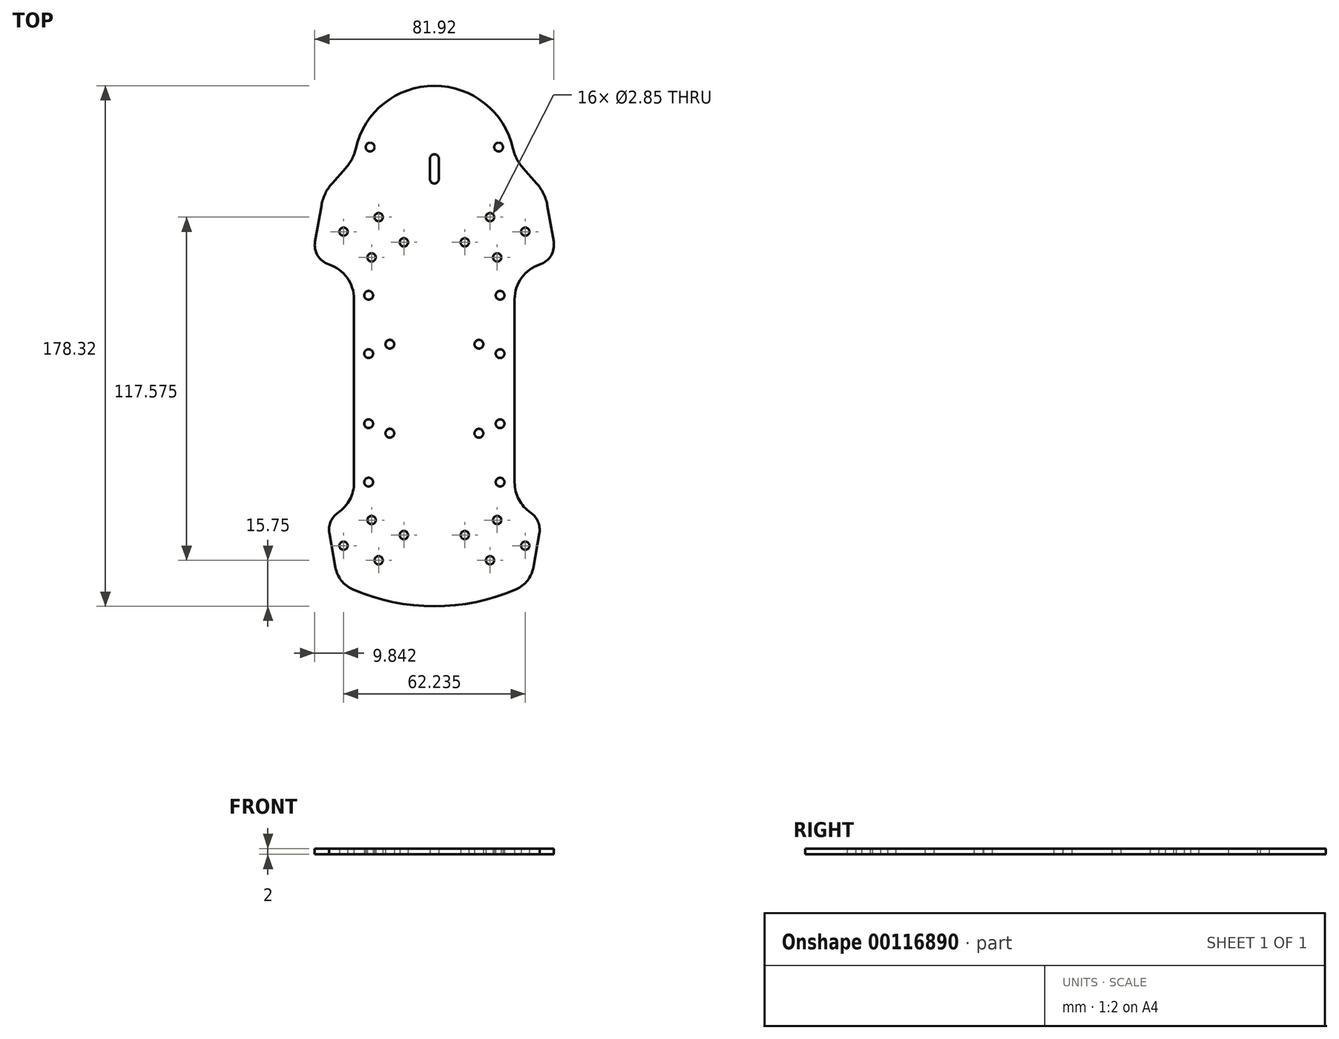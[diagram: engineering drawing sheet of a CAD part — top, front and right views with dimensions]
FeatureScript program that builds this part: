
annotation { "Feature Type Name" : "Feature", "Feature Type Description" : "" }
export const myFeature = defineFeature(function(context is Context, id is Id, definition is map)
    precondition{}
    {
        {
            var Q0;
            Q0=qCreatedBy(makeId("Top.planeOp"),FACE);
            var sketch = newSketch(context, id + "F0", { "sketchPlane" : qUnion([Q0])});
            skLineSegment(sketch, "E0", {"start": v(-27.15, 153.46) * mm, "end": v(-17.3, 155.2) * mm});
            skLineSegment(sketch, "E1", {"start": v(-17.3, 155.2) * mm, "end": v(-14.87, 141.4) * mm});
            skLineSegment(sketch, "E2", {"start": v(-14.87, 141.4) * mm, "end": v(-24.72, 139.67) * mm});
            skLineSegment(sketch, "E3", {"start": v(-24.72, 139.67) * mm, "end": v(-27.15, 153.46) * mm});
            skLineSegment(sketch, "E4", {"start": v(-8.87, 175.2) * mm, "end": v(-8.87, 29.62) * mm});
            skLineSegment(sketch, "E5", {"start": v(-63.87, 175.2) * mm, "end": v(-63.87, 29.62) * mm});
            skCircle(sketch, "E6", {"center": v(-51.62, 111.66) * mm, "radius": 1.5 * mm});
            skCircle(sketch, "E7", {"center": v(-21.12, 111.66) * mm, "radius": 1.5 * mm});
            skCircle(sketch, "E8", {"center": v(-51.62, 81.16) * mm, "radius": 1.5 * mm});
            skCircle(sketch, "E9", {"center": v(-21.12, 81.16) * mm, "radius": 1.5 * mm});
            skCircle(sketch, "E10", {"center": v(-17.3, 155.2) * mm, "radius": 1.43 * mm});
            skCircle(sketch, "E11", {"center": v(-27.15, 153.46) * mm, "radius": 1.43 * mm});
            skCircle(sketch, "E12", {"center": v(-24.72, 139.67) * mm, "radius": 1.43 * mm});
            skCircle(sketch, "E13", {"center": v(-14.87, 141.4) * mm, "radius": 1.43 * mm});
            skLineSegment(sketch, "E14", {"start": v(-63.87, 175.2) * mm, "end": v(-8.87, 175.2) * mm});
            skLineSegment(sketch, "E15", {"start": v(-45.6, 153.46) * mm, "end": v(-55.44, 155.2) * mm});
            skLineSegment(sketch, "E16", {"start": v(-55.44, 155.2) * mm, "end": v(-57.87, 141.4) * mm});
            skLineSegment(sketch, "E17", {"start": v(-57.87, 141.4) * mm, "end": v(-48.02, 139.67) * mm});
            skLineSegment(sketch, "E18", {"start": v(-48.02, 139.67) * mm, "end": v(-45.6, 153.46) * mm});
            skCircle(sketch, "E19", {"center": v(-55.44, 155.2) * mm, "radius": 1.43 * mm});
            skCircle(sketch, "E20", {"center": v(-45.6, 153.46) * mm, "radius": 1.43 * mm});
            skCircle(sketch, "E21", {"center": v(-48.02, 139.67) * mm, "radius": 1.43 * mm});
            skCircle(sketch, "E22", {"center": v(-57.87, 141.4) * mm, "radius": 1.43 * mm});
            skLineSegment(sketch, "E23", {"start": v(-63.87, 29.62) * mm, "end": v(-8.87, 29.62) * mm});
            skLineSegment(sketch, "E24.bottom", {"start": v(-54.37, 114.4) * mm, "end": v(-18.37, 114.4) * mm});
            skLineSegment(sketch, "E24.top", {"start": v(-54.37, 78.4) * mm, "end": v(-18.37, 78.4) * mm});
            skLineSegment(sketch, "E24.left", {"start": v(-54.37, 114.4) * mm, "end": v(-54.37, 78.4) * mm});
            skLineSegment(sketch, "E24.right", {"start": v(-18.37, 114.4) * mm, "end": v(-18.37, 78.4) * mm});
            skLineSegment(sketch, "E25", {"start": v(-57.87, 51.4) * mm, "end": v(-48.02, 53.14) * mm});
            skLineSegment(sketch, "E26", {"start": v(-48.02, 53.14) * mm, "end": v(-45.6, 39.36) * mm});
            skLineSegment(sketch, "E27", {"start": v(-45.6, 39.36) * mm, "end": v(-55.44, 37.62) * mm});
            skLineSegment(sketch, "E28", {"start": v(-55.44, 37.62) * mm, "end": v(-57.87, 51.4) * mm});
            skLineSegment(sketch, "E29", {"start": v(-24.72, 53.14) * mm, "end": v(-14.87, 51.4) * mm});
            skLineSegment(sketch, "E30", {"start": v(-14.87, 51.4) * mm, "end": v(-17.3, 37.62) * mm});
            skLineSegment(sketch, "E31", {"start": v(-17.3, 37.62) * mm, "end": v(-27.15, 39.36) * mm});
            skLineSegment(sketch, "E32", {"start": v(-27.15, 39.36) * mm, "end": v(-24.72, 53.14) * mm});
            skCircle(sketch, "E33", {"center": v(-57.87, 51.4) * mm, "radius": 1.43 * mm});
            skCircle(sketch, "E34", {"center": v(-48.02, 53.14) * mm, "radius": 1.43 * mm});
            skCircle(sketch, "E35", {"center": v(-45.6, 39.36) * mm, "radius": 1.43 * mm});
            skCircle(sketch, "E36", {"center": v(-55.44, 37.62) * mm, "radius": 1.43 * mm});
            skCircle(sketch, "E37", {"center": v(-27.15, 39.36) * mm, "radius": 1.43 * mm});
            skCircle(sketch, "E38", {"center": v(-24.72, 53.14) * mm, "radius": 1.43 * mm});
            skCircle(sketch, "E39", {"center": v(-14.87, 51.4) * mm, "radius": 1.43 * mm});
            skCircle(sketch, "E40", {"center": v(-17.3, 37.62) * mm, "radius": 1.43 * mm});
            skLineSegment(sketch, "E41", {"start": v(-74.29, 163.48) * mm, "end": v(-39.3, 157.93) * mm});
            skLineSegment(sketch, "E42", {"start": v(-39.3, 157.93) * mm, "end": v(-43.63, 133.31) * mm});
            skLineSegment(sketch, "E43", {"start": v(-43.63, 133.31) * mm, "end": v(-71.66, 138.76) * mm});
            skLineSegment(sketch, "E44", {"start": v(-77.22, 146.85) * mm, "end": v(-75.03, 159.3) * mm});
            skLineSegment(sketch, "E45", {"start": v(-36.37, 175.2) * mm, "end": v(-36.37, 125.27) * mm});
            skLineSegment(sketch, "E46.MirrorCS", {"start": v(1.55, 163.48) * mm, "end": v(-33.45, 157.93) * mm});
            skLineSegment(sketch, "E47.MirrorCS", {"start": v(-33.45, 157.93) * mm, "end": v(-29.1, 133.31) * mm});
            skLineSegment(sketch, "E48.MirrorCS", {"start": v(-29.1, 133.31) * mm, "end": v(-1.08, 138.76) * mm});
            skLineSegment(sketch, "E49.MirrorCS", {"start": v(4.48, 146.85) * mm, "end": v(2.28, 159.3) * mm});
            skPoint(sketch, "E50", {"position": v(-36.37, 200.2) * mm});
            skArc(sketch, "E51", {"start": v(-9.42, 178.63) * mm, "mid": v(-36.37, 200.2) * mm, "end": v(-63.32, 178.63) * mm});
            skLineSegment(sketch, "E52", {"start": v(-71.46, 166.65) * mm, "end": v(-66.74, 171.96) * mm});
            skLineSegment(sketch, "E53", {"start": v(-6, 171.96) * mm, "end": v(-1.28, 166.65) * mm});
            skCircle(sketch, "E54", {"center": v(-36.37, 175.2) * mm, "radius": 1.5 * mm});
            skPoint(sketch, "E55.visualSharp", {"position": v(-78.41, 140.07) * mm});
            skArc(sketch, "E55.filletArc", {"start": v(-77.22, 146.85) * mm, "mid": v(-76.1, 141.67) * mm, "end": v(-71.66, 138.76) * mm});
            skPoint(sketch, "E56.visualSharp", {"position": v(5.67, 140.07) * mm});
            skArc(sketch, "E56.filletArc", {"start": v(-1.08, 138.76) * mm, "mid": v(3.35, 141.67) * mm, "end": v(4.48, 146.85) * mm});
            skPoint(sketch, "E57.visualSharp", {"position": v(-74.29, 163.48) * mm});
            skArc(sketch, "E57.filletArc", {"start": v(-71.46, 166.65) * mm, "mid": v(-73.76, 163.22) * mm, "end": v(-75.03, 159.3) * mm});
            skPoint(sketch, "E58.visualSharp", {"position": v(-63.87, 175.2) * mm});
            skArc(sketch, "E58.filletArc", {"start": v(-66.74, 171.96) * mm, "mid": v(-64.6, 175.08) * mm, "end": v(-63.32, 178.63) * mm});
            skPoint(sketch, "E59.visualSharp", {"position": v(-8.87, 175.2) * mm});
            skArc(sketch, "E59.filletArc", {"start": v(-9.42, 178.63) * mm, "mid": v(-8.13, 175.08) * mm, "end": v(-6, 171.96) * mm});
            skPoint(sketch, "E60.visualSharp", {"position": v(1.55, 163.48) * mm});
            skArc(sketch, "E60.filletArc", {"start": v(2.28, 159.3) * mm, "mid": v(1.02, 163.22) * mm, "end": v(-1.28, 166.65) * mm});
            skCircle(sketch, "E61", {"center": v(-76.37, 127.1) * mm, "radius": 12.5 * mm});
            skCircle(sketch, "E62", {"center": v(3.63, 127.1) * mm, "radius": 12.5 * mm});
            skLineSegment(sketch, "E63", {"start": v(-54.37, 96.4) * mm, "end": v(-95.75, 96.4) * mm});
            skPoint(sketch, "E63.endSnap0", {"position": v(-54.37, 96.4) * mm});
            skLineSegment(sketch, "E64.MirrorCS", {"start": v(-33.45, 34.88) * mm, "end": v(-29.1, 59.5) * mm});
            skLineSegment(sketch, "E65", {"start": v(-29.1, 59.5) * mm, "end": v(-5.99, 55) * mm});
            skLineSegment(sketch, "E66", {"start": v(-0.43, 46.92) * mm, "end": v(-2.5, 35.15) * mm});
            skLineSegment(sketch, "E67", {"start": v(-3.4, 30.12) * mm, "end": v(-33.45, 34.88) * mm});
            skLineSegment(sketch, "E68.MirrorCS", {"start": v(-39.3, 34.88) * mm, "end": v(-43.63, 59.5) * mm});
            skLineSegment(sketch, "E69.MirrorCS", {"start": v(-43.63, 59.5) * mm, "end": v(-66.75, 55) * mm});
            skLineSegment(sketch, "E70.MirrorCS", {"start": v(-69.35, 30.12) * mm, "end": v(-39.3, 34.88) * mm});
            skLineSegment(sketch, "E71.MirrorCS", {"start": v(-72.31, 46.92) * mm, "end": v(-70.23, 35.15) * mm});
            skArc(sketch, "E72", {"start": v(-64.39, 27.72) * mm, "mid": v(-36.37, 21.87) * mm, "end": v(-8.35, 27.72) * mm});
            skCircle(sketch, "E73", {"center": v(-76.37, 64.27) * mm, "radius": 12.5 * mm});
            skCircle(sketch, "E74", {"center": v(3.63, 64.27) * mm, "radius": 12.5 * mm});
            skPoint(sketch, "E75.visualSharp", {"position": v(-73.5, 53.7) * mm});
            skArc(sketch, "E75.filletArc", {"start": v(-66.75, 55) * mm, "mid": v(-71.19, 52.1) * mm, "end": v(-72.31, 46.92) * mm});
            skPoint(sketch, "E76.visualSharp", {"position": v(0.76, 53.7) * mm});
            skArc(sketch, "E76.filletArc", {"start": v(-0.43, 46.92) * mm, "mid": v(-1.55, 52.1) * mm, "end": v(-5.99, 55) * mm});
            skPoint(sketch, "E77.visualSharp", {"position": v(-69.35, 30.12) * mm});
            skArc(sketch, "E77.filletArc", {"start": v(-70.23, 35.15) * mm, "mid": v(-68.24, 30.7) * mm, "end": v(-64.39, 27.72) * mm});
            skPoint(sketch, "E78.visualSharp", {"position": v(-3.4, 30.12) * mm});
            skArc(sketch, "E78.filletArc", {"start": v(-8.35, 27.72) * mm, "mid": v(-4.5, 30.7) * mm, "end": v(-2.5, 35.15) * mm});
            skCircle(sketch, "E79", {"center": v(-58.87, 128.4) * mm, "radius": 1.5 * mm});
            skCircle(sketch, "E80", {"center": v(-58.87, 108.4) * mm, "radius": 1.5 * mm});
            skCircle(sketch, "E81", {"center": v(-58.87, 84.4) * mm, "radius": 1.5 * mm});
            skCircle(sketch, "E82", {"center": v(-58.87, 64.4) * mm, "radius": 1.5 * mm});
            skCircle(sketch, "E83.MirrorC", {"center": v(-13.87, 128.4) * mm, "radius": 1.5 * mm});
            skCircle(sketch, "E84.MirrorC", {"center": v(-13.87, 108.4) * mm, "radius": 1.5 * mm});
            skCircle(sketch, "E85.MirrorC", {"center": v(-13.87, 84.4) * mm, "radius": 1.5 * mm});
            skCircle(sketch, "E86.MirrorC", {"center": v(-13.87, 64.4) * mm, "radius": 1.5 * mm});
            skCircle(sketch, "E87", {"center": v(-58.37, 179.2) * mm, "radius": 1.5 * mm});
            skCircle(sketch, "E88", {"center": v(-14.37, 179.2) * mm, "radius": 1.5 * mm});
            skLineSegment(sketch, "E89", {"start": v(-56.65, 148.3) * mm, "end": v(-67.49, 150.21) * mm});
            skCircle(sketch, "E90", {"center": v(-67.49, 150.21) * mm, "radius": 1.43 * mm});
            skCircle(sketch, "E91.MirrorC", {"center": v(-5.25, 150.21) * mm, "radius": 1.43 * mm});
            skCircle(sketch, "E92.MirrorC", {"center": v(-67.49, 42.6) * mm, "radius": 1.43 * mm});
            skCircle(sketch, "E93.MirrorC", {"center": v(-5.25, 42.6) * mm, "radius": 1.43 * mm});
            skCircle(sketch, "E94", {"center": v(-46.8, 146.56) * mm, "radius": 1.43 * mm});
            skCircle(sketch, "E95.MirrorC", {"center": v(-25.93, 146.56) * mm, "radius": 1.43 * mm});
            skCircle(sketch, "E96.MirrorC", {"center": v(-46.8, 46.25) * mm, "radius": 1.43 * mm});
            skCircle(sketch, "E97.MirrorC", {"center": v(-25.93, 46.25) * mm, "radius": 1.43 * mm});
            skCircle(sketch, "E98", {"center": v(-36.37, 168.2) * mm, "radius": 1.5 * mm});
            skLineSegment(sketch, "E99", {"start": v(-37.87, 178.57) * mm, "end": v(-37.87, 162.7) * mm});
            skLineSegment(sketch, "E100", {"start": v(-34.87, 178.97) * mm, "end": v(-34.87, 161.55) * mm});
            skSolve(sketch);
        }
        {
            var Q0;
            Q0=makeQuery(id+"F0.imprint","IMPRINT",FACE,{"disambiguationData":[TD([[makeQuery(id+"F0.imprint","IMPRINT",EDGE,{"derivedFrom":sQuery(id+"F0.wireOp",EDGE,"E23")}),-1.0]])]});
            var Q1;
            {var subQ0=sQuery(id+"F0.wireOp",EDGE,"E62");var subQ1=sQuery(id+"F0.wireOp",EDGE,"E56.filletArc");var subQ3=makeQuery(id+"F0.imprint","INTERSECT",VERTEX,{"derivedFrom":[subQ1,subQ0]});Q1=makeQuery(id+"F0.imprint","IMPRINT",FACE,{"disambiguationData":[TD([[makeQuery(id+"F0.imprint","IMPRINT",EDGE,{"disambiguationData":[TD([[subQ3,1.0]])],"derivedFrom":subQ1}),1.0]])]});}
            var Q2;
            {var subQ0=sQuery(id+"F0.wireOp",EDGE,"E62");var subQ1=sQuery(id+"F0.wireOp",EDGE,"E4");var subQ2=makeQuery(id+"F0.imprint","INTERSECT",VERTEX,{"derivedFrom":[subQ1,subQ0]});Q2=makeQuery(id+"F0.imprint","IMPRINT",FACE,{"disambiguationData":[TD([[makeQuery(id+"F0.imprint","IMPRINT",EDGE,{"disambiguationData":[TD([[subQ2,1.0]])],"derivedFrom":subQ1}),1.0]])]});}
            var Q3;
            {var subQ0=sQuery(id+"F0.wireOp",EDGE,"E61");var subQ1=sQuery(id+"F0.wireOp",EDGE,"E5");var subQ2=makeQuery(id+"F0.imprint","INTERSECT",VERTEX,{"derivedFrom":[subQ1,subQ0]});Q3=makeQuery(id+"F0.imprint","IMPRINT",FACE,{"disambiguationData":[TD([[makeQuery(id+"F0.imprint","IMPRINT",EDGE,{"disambiguationData":[TD([[subQ2,1.0]])],"derivedFrom":subQ1}),-1.0]])]});}
            var Q4;
            Q4=makeQuery(id+"F0.imprint","IMPRINT",FACE,{"disambiguationData":[TD([[makeQuery(id+"F0.imprint","IMPRINT",EDGE,{"derivedFrom":sQuery(id+"F0.wireOp",EDGE,"E51")}),1.0]])]});
            var Q5;
            {var subQ0=sQuery(id+"F0.wireOp",EDGE,"E49.MirrorCS");Q5=makeQuery(id+"F0.imprint","IMPRINT",FACE,{"disambiguationData":[TD([[makeQuery(id+"F0.imprint","IMPRINT",EDGE,{"derivedFrom":subQ0}),1.0]])]});}
            var Q6;
            {var subQ0=sQuery(id+"F0.wireOp",EDGE,"E44");Q6=makeQuery(id+"F0.imprint","IMPRINT",FACE,{"disambiguationData":[TD([[makeQuery(id+"F0.imprint","IMPRINT",EDGE,{"derivedFrom":subQ0}),-1.0]])]});}
            var Q7;
            {var subQ29=sQuery(id+"F0.wireOp",EDGE,"E23");Q7=makeQuery(id+"F0.imprint","IMPRINT",FACE,{"disambiguationData":[TD([[makeQuery(id+"F0.imprint","IMPRINT",EDGE,{"derivedFrom":subQ29}),1.0]])]});}
            var Q8;
            {var subQ3=sQuery(id+"F0.wireOp",EDGE,"E20");var subQ13=sQuery(id+"F0.wireOp",EDGE,"E15");var subQ14=makeQuery(id+"F0.imprint","INTERSECT",VERTEX,{"derivedFrom":[subQ13,subQ3]});Q8=makeQuery(id+"F0.imprint","IMPRINT",FACE,{"disambiguationData":[TD([[makeQuery(id+"F0.imprint","IMPRINT",EDGE,{"disambiguationData":[TD([[subQ14,-1.0]])],"derivedFrom":subQ13}),1.0]])]});}
            var Q9;
            {var subQ3=sQuery(id+"F0.wireOp",EDGE,"E11");var subQ13=sQuery(id+"F0.wireOp",EDGE,"E0");var subQ14=makeQuery(id+"F0.imprint","INTERSECT",VERTEX,{"derivedFrom":[subQ13,subQ3]});Q9=makeQuery(id+"F0.imprint","IMPRINT",FACE,{"disambiguationData":[TD([[makeQuery(id+"F0.imprint","IMPRINT",EDGE,{"disambiguationData":[TD([[subQ14,-1.0]])],"derivedFrom":subQ13}),-1.0]])]});}
            var Q10;
            Q10=makeQuery(id+"F0.imprint","IMPRINT",FACE,{"disambiguationData":[TD([[makeQuery(id+"F0.imprint","IMPRINT",EDGE,{"derivedFrom":sQuery(id+"F0.wireOp",EDGE,"E6")}),-1.0]])]});
            var Q11;
            {var subQ3=sQuery(id+"F0.wireOp",EDGE,"E33");var subQ13=sQuery(id+"F0.wireOp",EDGE,"E25");var subQ14=makeQuery(id+"F0.imprint","INTERSECT",VERTEX,{"derivedFrom":[subQ13,subQ3]});Q11=makeQuery(id+"F0.imprint","IMPRINT",FACE,{"disambiguationData":[TD([[makeQuery(id+"F0.imprint","IMPRINT",EDGE,{"disambiguationData":[TD([[subQ14,-1.0]])],"derivedFrom":subQ13}),-1.0]])]});}
            var Q12;
            {var subQ3=sQuery(id+"F0.wireOp",EDGE,"E38");var subQ13=sQuery(id+"F0.wireOp",EDGE,"E29");var subQ14=makeQuery(id+"F0.imprint","INTERSECT",VERTEX,{"derivedFrom":[subQ13,subQ3]});Q12=makeQuery(id+"F0.imprint","IMPRINT",FACE,{"disambiguationData":[TD([[makeQuery(id+"F0.imprint","IMPRINT",EDGE,{"disambiguationData":[TD([[subQ14,-1.0]])],"derivedFrom":subQ13}),-1.0]])]});}
            var Q13;
            {var subQ0=sQuery(id+"F0.wireOp",EDGE,"E42");Q13=makeQuery(id+"F0.imprint","IMPRINT",FACE,{"disambiguationData":[TD([[makeQuery(id+"F0.imprint","IMPRINT",EDGE,{"derivedFrom":subQ0}),-1.0]])]});}
            var Q14;
            {var subQ0=sQuery(id+"F0.wireOp",EDGE,"E47.MirrorCS");Q14=makeQuery(id+"F0.imprint","IMPRINT",FACE,{"disambiguationData":[TD([[makeQuery(id+"F0.imprint","IMPRINT",EDGE,{"derivedFrom":subQ0}),1.0]])]});}
            var Q15;
            {var subQ0=sQuery(id+"F0.wireOp",EDGE,"E61");var subQ1=sQuery(id+"F0.wireOp",EDGE,"E55.filletArc");var subQ3=makeQuery(id+"F0.imprint","INTERSECT",VERTEX,{"derivedFrom":[subQ1,subQ0]});Q15=makeQuery(id+"F0.imprint","IMPRINT",FACE,{"disambiguationData":[TD([[makeQuery(id+"F0.imprint","IMPRINT",EDGE,{"disambiguationData":[TD([[subQ3,-1.0]])],"derivedFrom":subQ1}),1.0]])]});}
            var Q16;
            {var subQ0=sQuery(id+"F0.wireOp",EDGE,"E74");var subQ1=sQuery(id+"F0.wireOp",EDGE,"E4");var subQ2=makeQuery(id+"F0.imprint","INTERSECT",VERTEX,{"derivedFrom":[subQ1,subQ0]});Q16=makeQuery(id+"F0.imprint","IMPRINT",FACE,{"disambiguationData":[TD([[makeQuery(id+"F0.imprint","IMPRINT",EDGE,{"disambiguationData":[TD([[subQ2,-1.0]])],"derivedFrom":subQ1}),1.0]])]});}
            var Q17;
            {var subQ10=sQuery(id+"F0.wireOp",EDGE,"E66");Q17=makeQuery(id+"F0.imprint","IMPRINT",FACE,{"disambiguationData":[TD([[makeQuery(id+"F0.imprint","IMPRINT",EDGE,{"derivedFrom":subQ10}),-1.0]])]});}
            var Q18;
            {var subQ0=sQuery(id+"F0.wireOp",EDGE,"E64.MirrorCS");Q18=makeQuery(id+"F0.imprint","IMPRINT",FACE,{"disambiguationData":[TD([[makeQuery(id+"F0.imprint","IMPRINT",EDGE,{"derivedFrom":subQ0}),-1.0]])]});}
            var Q19;
            {var subQ0=sQuery(id+"F0.wireOp",EDGE,"E68.MirrorCS");Q19=makeQuery(id+"F0.imprint","IMPRINT",FACE,{"disambiguationData":[TD([[makeQuery(id+"F0.imprint","IMPRINT",EDGE,{"derivedFrom":subQ0}),1.0]])]});}
            var Q20;
            {var subQ0=sQuery(id+"F0.wireOp",EDGE,"E71.MirrorCS");Q20=makeQuery(id+"F0.imprint","IMPRINT",FACE,{"disambiguationData":[TD([[makeQuery(id+"F0.imprint","IMPRINT",EDGE,{"derivedFrom":subQ0}),1.0]])]});}
            var Q21;
            {var subQ0=sQuery(id+"F0.wireOp",EDGE,"E73");var subQ1=sQuery(id+"F0.wireOp",EDGE,"E5");var subQ2=makeQuery(id+"F0.imprint","INTERSECT",VERTEX,{"derivedFrom":[subQ1,subQ0]});Q21=makeQuery(id+"F0.imprint","IMPRINT",FACE,{"disambiguationData":[TD([[makeQuery(id+"F0.imprint","IMPRINT",EDGE,{"disambiguationData":[TD([[subQ2,-1.0]])],"derivedFrom":subQ1}),-1.0]])]});}
            var Q22;
            {var subQ0=sQuery(id+"F0.wireOp",EDGE,"E18");var subQ1=sQuery(id+"F0.wireOp",EDGE,"E15");var subQ2=makeQuery(id+"F0.imprint","INTERSECT",VERTEX,{"derivedFrom":[subQ1,subQ0]});Q22=makeQuery(id+"F0.imprint","IMPRINT",FACE,{"disambiguationData":[TD([[makeQuery(id+"F0.imprint","IMPRINT",EDGE,{"disambiguationData":[TD([[subQ2,-1.0]])],"derivedFrom":subQ1}),1.0]])]});}
            var Q23;
            {var subQ0=sQuery(id+"F0.wireOp",EDGE,"E18");var subQ1=sQuery(id+"F0.wireOp",EDGE,"E15");var subQ2=makeQuery(id+"F0.imprint","INTERSECT",VERTEX,{"derivedFrom":[subQ1,subQ0]});Q23=makeQuery(id+"F0.imprint","IMPRINT",FACE,{"disambiguationData":[TD([[makeQuery(id+"F0.imprint","IMPRINT",EDGE,{"disambiguationData":[TD([[subQ2,-1.0]])],"derivedFrom":subQ1}),-1.0]])]});}
            var Q24;
            {var subQ0=sQuery(id+"F0.wireOp",EDGE,"E18");var subQ1=sQuery(id+"F0.wireOp",EDGE,"E17");var subQ2=makeQuery(id+"F0.imprint","INTERSECT",VERTEX,{"derivedFrom":[subQ1,subQ0]});Q24=makeQuery(id+"F0.imprint","IMPRINT",FACE,{"disambiguationData":[TD([[makeQuery(id+"F0.imprint","IMPRINT",EDGE,{"disambiguationData":[TD([[subQ2,1.0]])],"derivedFrom":subQ1}),1.0]])]});}
            var Q25;
            {var subQ0=sQuery(id+"F0.wireOp",EDGE,"E18");var subQ1=sQuery(id+"F0.wireOp",EDGE,"E17");var subQ2=makeQuery(id+"F0.imprint","INTERSECT",VERTEX,{"derivedFrom":[subQ1,subQ0]});Q25=makeQuery(id+"F0.imprint","IMPRINT",FACE,{"disambiguationData":[TD([[makeQuery(id+"F0.imprint","IMPRINT",EDGE,{"disambiguationData":[TD([[subQ2,1.0]])],"derivedFrom":subQ1}),-1.0]])]});}
            var Q26;
            {var subQ0=sQuery(id+"F0.wireOp",EDGE,"E3");var subQ1=sQuery(id+"F0.wireOp",EDGE,"E0");var subQ2=makeQuery(id+"F0.imprint","INTERSECT",VERTEX,{"derivedFrom":[subQ1,subQ0]});Q26=makeQuery(id+"F0.imprint","IMPRINT",FACE,{"disambiguationData":[TD([[makeQuery(id+"F0.imprint","IMPRINT",EDGE,{"disambiguationData":[TD([[subQ2,-1.0]])],"derivedFrom":subQ1}),-1.0]])]});}
            var Q27;
            {var subQ0=sQuery(id+"F0.wireOp",EDGE,"E3");var subQ1=sQuery(id+"F0.wireOp",EDGE,"E0");var subQ2=makeQuery(id+"F0.imprint","INTERSECT",VERTEX,{"derivedFrom":[subQ1,subQ0]});Q27=makeQuery(id+"F0.imprint","IMPRINT",FACE,{"disambiguationData":[TD([[makeQuery(id+"F0.imprint","IMPRINT",EDGE,{"disambiguationData":[TD([[subQ2,-1.0]])],"derivedFrom":subQ1}),1.0]])]});}
            var Q28;
            {var subQ0=sQuery(id+"F0.wireOp",EDGE,"E3");var subQ1=sQuery(id+"F0.wireOp",EDGE,"E2");var subQ2=makeQuery(id+"F0.imprint","INTERSECT",VERTEX,{"derivedFrom":[subQ1,subQ0]});Q28=makeQuery(id+"F0.imprint","IMPRINT",FACE,{"disambiguationData":[TD([[makeQuery(id+"F0.imprint","IMPRINT",EDGE,{"disambiguationData":[TD([[subQ2,1.0]])],"derivedFrom":subQ1}),1.0]])]});}
            var Q29;
            {var subQ0=sQuery(id+"F0.wireOp",EDGE,"E3");var subQ1=sQuery(id+"F0.wireOp",EDGE,"E2");var subQ2=makeQuery(id+"F0.imprint","INTERSECT",VERTEX,{"derivedFrom":[subQ1,subQ0]});Q29=makeQuery(id+"F0.imprint","IMPRINT",FACE,{"disambiguationData":[TD([[makeQuery(id+"F0.imprint","IMPRINT",EDGE,{"disambiguationData":[TD([[subQ2,1.0]])],"derivedFrom":subQ1}),-1.0]])]});}
            var Q30;
            {var subQ0=sQuery(id+"F0.wireOp",EDGE,"E26");var subQ1=sQuery(id+"F0.wireOp",EDGE,"E25");var subQ2=makeQuery(id+"F0.imprint","INTERSECT",VERTEX,{"derivedFrom":[subQ1,subQ0]});Q30=makeQuery(id+"F0.imprint","IMPRINT",FACE,{"disambiguationData":[TD([[makeQuery(id+"F0.imprint","IMPRINT",EDGE,{"disambiguationData":[TD([[subQ2,1.0]])],"derivedFrom":subQ1}),1.0]])]});}
            var Q31;
            {var subQ0=sQuery(id+"F0.wireOp",EDGE,"E26");var subQ1=sQuery(id+"F0.wireOp",EDGE,"E25");var subQ2=makeQuery(id+"F0.imprint","INTERSECT",VERTEX,{"derivedFrom":[subQ1,subQ0]});Q31=makeQuery(id+"F0.imprint","IMPRINT",FACE,{"disambiguationData":[TD([[makeQuery(id+"F0.imprint","IMPRINT",EDGE,{"disambiguationData":[TD([[subQ2,1.0]])],"derivedFrom":subQ1}),-1.0]])]});}
            var Q32;
            {var subQ0=sQuery(id+"F0.wireOp",EDGE,"E27");var subQ1=sQuery(id+"F0.wireOp",EDGE,"E26");var subQ2=makeQuery(id+"F0.imprint","INTERSECT",VERTEX,{"derivedFrom":[subQ1,subQ0]});Q32=makeQuery(id+"F0.imprint","IMPRINT",FACE,{"disambiguationData":[TD([[makeQuery(id+"F0.imprint","IMPRINT",EDGE,{"disambiguationData":[TD([[subQ2,1.0]])],"derivedFrom":subQ1}),-1.0]])]});}
            var Q33;
            {var subQ0=sQuery(id+"F0.wireOp",EDGE,"E27");var subQ1=sQuery(id+"F0.wireOp",EDGE,"E26");var subQ2=makeQuery(id+"F0.imprint","INTERSECT",VERTEX,{"derivedFrom":[subQ1,subQ0]});Q33=makeQuery(id+"F0.imprint","IMPRINT",FACE,{"disambiguationData":[TD([[makeQuery(id+"F0.imprint","IMPRINT",EDGE,{"disambiguationData":[TD([[subQ2,1.0]])],"derivedFrom":subQ1}),1.0]])]});}
            var Q34;
            {var subQ0=sQuery(id+"F0.wireOp",EDGE,"E32");var subQ1=sQuery(id+"F0.wireOp",EDGE,"E29");var subQ2=makeQuery(id+"F0.imprint","INTERSECT",VERTEX,{"derivedFrom":[subQ1,subQ0]});Q34=makeQuery(id+"F0.imprint","IMPRINT",FACE,{"disambiguationData":[TD([[makeQuery(id+"F0.imprint","IMPRINT",EDGE,{"disambiguationData":[TD([[subQ2,-1.0]])],"derivedFrom":subQ1}),1.0]])]});}
            var Q35;
            {var subQ0=sQuery(id+"F0.wireOp",EDGE,"E32");var subQ1=sQuery(id+"F0.wireOp",EDGE,"E29");var subQ2=makeQuery(id+"F0.imprint","INTERSECT",VERTEX,{"derivedFrom":[subQ1,subQ0]});Q35=makeQuery(id+"F0.imprint","IMPRINT",FACE,{"disambiguationData":[TD([[makeQuery(id+"F0.imprint","IMPRINT",EDGE,{"disambiguationData":[TD([[subQ2,-1.0]])],"derivedFrom":subQ1}),-1.0]])]});}
            var Q36;
            {var subQ0=sQuery(id+"F0.wireOp",EDGE,"E32");var subQ1=sQuery(id+"F0.wireOp",EDGE,"E31");var subQ2=makeQuery(id+"F0.imprint","INTERSECT",VERTEX,{"derivedFrom":[subQ1,subQ0]});Q36=makeQuery(id+"F0.imprint","IMPRINT",FACE,{"disambiguationData":[TD([[makeQuery(id+"F0.imprint","IMPRINT",EDGE,{"disambiguationData":[TD([[subQ2,1.0]])],"derivedFrom":subQ1}),-1.0]])]});}
            var Q37;
            {var subQ0=sQuery(id+"F0.wireOp",EDGE,"E32");var subQ1=sQuery(id+"F0.wireOp",EDGE,"E31");var subQ2=makeQuery(id+"F0.imprint","INTERSECT",VERTEX,{"derivedFrom":[subQ1,subQ0]});Q37=makeQuery(id+"F0.imprint","IMPRINT",FACE,{"disambiguationData":[TD([[makeQuery(id+"F0.imprint","IMPRINT",EDGE,{"disambiguationData":[TD([[subQ2,1.0]])],"derivedFrom":subQ1}),1.0]])]});}
            extrude(context, id + "F1", {"entities" : qUnion([Q0, Q1, Q2, Q3, Q4, Q5, Q6, Q7, Q8, Q9, Q10, Q11, Q12, Q13, Q14, Q15, Q16, Q17, Q18, Q19, Q20, Q21, Q22, Q23, Q24, Q25, Q26, Q27, Q28, Q29, Q30, Q31, Q32, Q33, Q34, Q35, Q36, Q37]), "depth" : 2 * mm});
        }
    });
